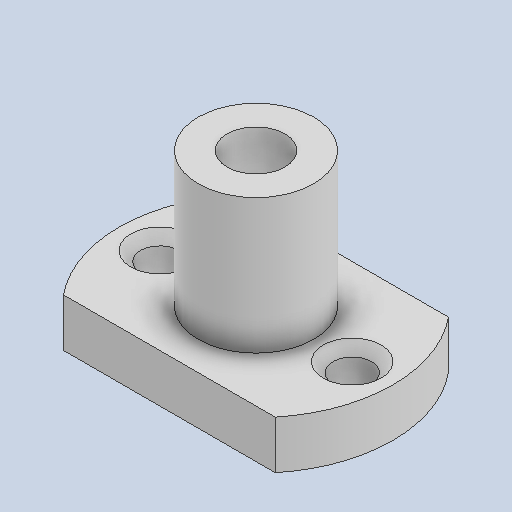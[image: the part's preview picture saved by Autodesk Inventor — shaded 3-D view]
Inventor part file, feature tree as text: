
AUTODESK INVENTOR PART (.ipt)
format: ipt  version: 2022 (Build 260153000, 153)  size: 126,464 bytes
history: native  units: in
note: dims shown in document units (in); Inventor stores cm internally (conversion verified against a paired STEP export)
features: chamfer x1
ambient origin geometry x8: Origin, YZ Plane, XZ Plane, XY Plane, X Axis, Y Axis, Z Axis, Center Point
bodies: Solid1 (feature_tree)
feature tree (1):
  chamfer  "Chamfer1"  [1 undecoded]
note: 1 required parameter value undecoded (feature->parameter linkage not recoverable at this tier; creation-order binding heuristic only, values carry confidence <= 0.55)
